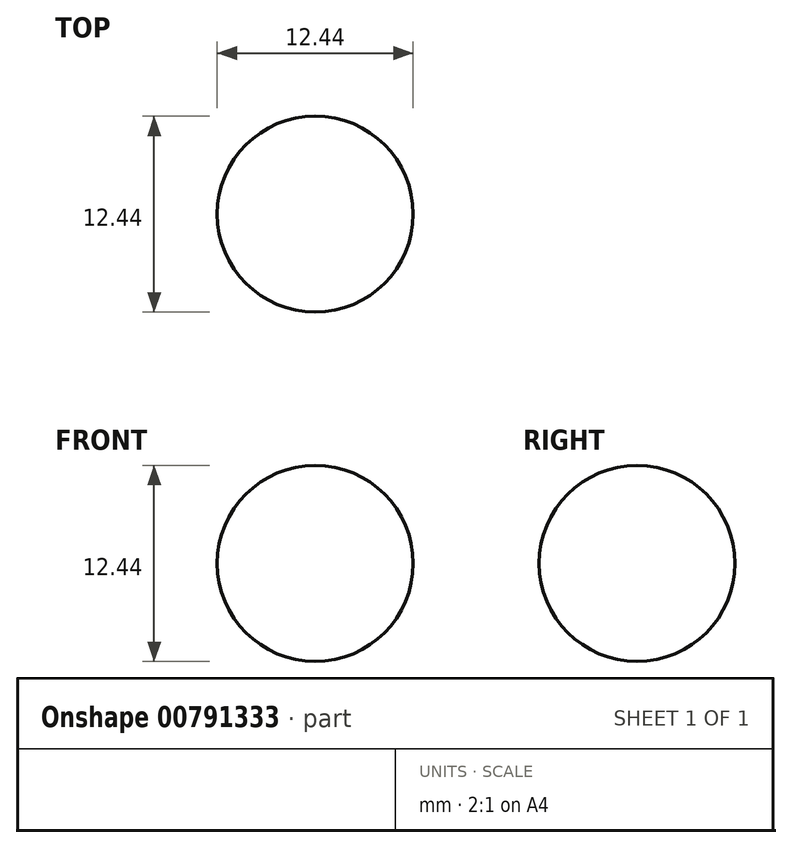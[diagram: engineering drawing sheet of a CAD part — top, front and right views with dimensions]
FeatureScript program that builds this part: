
annotation { "Feature Type Name" : "Feature", "Feature Type Description" : "" }
export const myFeature = defineFeature(function(context is Context, id is Id, definition is map)
    precondition{}
    {
        {
            var Q0;
            Q0=qCreatedBy(makeId("Front.planeOp"),FACE);
            var sketch = newSketch(context, id + "F0", { "sketchPlane" : qUnion([Q0])});
            skArc(sketch, "E0", {"start": v(0, -6.22) * mm, "mid": v(6.22, 0) * mm, "end": v(0, 6.22) * mm});
            skLineSegment(sketch, "E1", {"start": v(0, 6.22) * mm, "end": v(0, -6.22) * mm});
            skSolve(sketch);
        }
        {
            var Q0;
            Q0=makeQuery(id+"F0.imprint","IMPRINT",FACE,{"disambiguationData":[TD([[makeQuery(id+"F0.imprint","IMPRINT",EDGE,{"derivedFrom":sQuery(id+"F0.wireOp",EDGE,"E0")}),1.0]])]});
            var Q1;
            Q1=sQuery(id+"F0.wireOp",EDGE,"E1");
            revolve(context, id + "F1", {"entities" : qUnion([Q0]), "axis" : qUnion([Q1]), "revolveType" : RevolveType.FULL});
        }
    });
